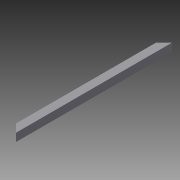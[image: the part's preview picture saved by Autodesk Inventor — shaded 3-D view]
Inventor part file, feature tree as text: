
AUTODESK INVENTOR PART (.ipt)
format: ipt  version: 2013 (Build 170138000, 138)  size: 86,528 bytes
history: native  units: in
note: dims shown in document units (in); Inventor stores cm internally (conversion verified against a paired STEP export)
features: extrude x2, sketch x2
ambient origin geometry x8: Origin, YZ Plane, XZ Plane, XY Plane, X Axis, Y Axis, Z Axis, Center Point
bodies: Solid1 (feature_tree)
feature tree (4):
  extrude  "Extrusion1"  Depth=1.0in
  extrude  "Extrusion2"  Depth=19.5in TaperAngle=0.0deg
  sketch  "Sketch1"  dims[d0=1.0in d2=1.0in]
  sketch  "Sketch2"  dims[d3=0.0625in d4=19.5in d5=0.0in d6=135.0deg d7=45.0deg d8=19.5in d9=0.0in]
